# Revit family: Absperrventil 4125 WD
name_source: partatom
category: Rohrzubehör
units: mm (PartAtom-declared; Revit-internal decimal feet)

## family parameters
Arbeitsebenenbasiert = Nein
Beim Laden mit Abzugskörper schneiden = Nein
Bemaßung runder Anschluss = Durchmesser verwenden
Gemeinsam genutzt = Nein
Immer vertikal = Ja
OmniClass-Nummer = 23.65.55.14
OmniClass-Titel = Valves for Liquid Services
Teiletyp = Unterbricht

## types (1)
- Absperrventil 4125 WD
    Anwendungsgebiet = Zum Absperren von Trinkwasserleitungen in Gebäuden.
    Dichtungen = EPDM nach KTW
    Gehäuse = entzinkungsbeständiges Gussmessing CC770S
    Gelegentliche Temperaturanstiege = bis 95°C, wenn sie nicht länger als 1 h andauern
    Handrad = Kunststoff, grün
    Hersteller = HERZ Armaturen Ges.m.b.H.
    Hinweis = Gemäß Art 33 der REACH-Verordnung (EG Nr. 1907/2006) sind wir verpflichtet, darauf hinzuweisen, dass der Stoff Blei auf der SVHC-Liste geführt wird und dass alle aus Messing bestehenden Bauteile, die in unseren Erzeugnissen verarbeitet sind, mehr als 0,1 % (w/w) Blei (CAS: 7439-92-1 / EINECS: 231-100-4) enthalten.
Da Blei als Legierungsbestandteil fest gebunden ist, sind keine Expositionen zu erwarten und daher sind keine zusätzlichen Angaben zur sicheren Verwendung notwendig.
    Kegel = entzinkungsbeständiges Messing CW626N
    L03 = 15 mm
    Max. Betriebsdruck = 2000000.0 Pa
    Max. Betriebsdruck (ÖVGW) = 1000000.0 Pa
    Max. Betriebstemperatur = 80 °C
    Max. Differenzdruck auf geschlossenen Sitz = 1000000.0 Pa
    Max. Gebrauchstemperatur (ÖVGW) = 65 °C
    Medium = Trinkwasser
    Oberteil = entzinkungsbeständiges Messing CW626N
    R03 = 10 mm  [stored 0.0328084 ft]
    R100 = 1 mm  [stored 0.00328084 ft]
    S03 = 60 mm  [stored 0.19685 ft]
    SCTWCODE = 04;00;02
    SCTWSEQ = FW_SBT_TYP_FW="109";2
    SC_NennweiteBerechnet = 0
    SW01 = 60.00°
    Spindel = Messing CW617N
    URL = www.herz-armaturen.at
    W01 = 45.00°

note: [stored X ft] marks values corroborated as IEEE doubles in the binary element streams (Revit-internal decimal feet)
